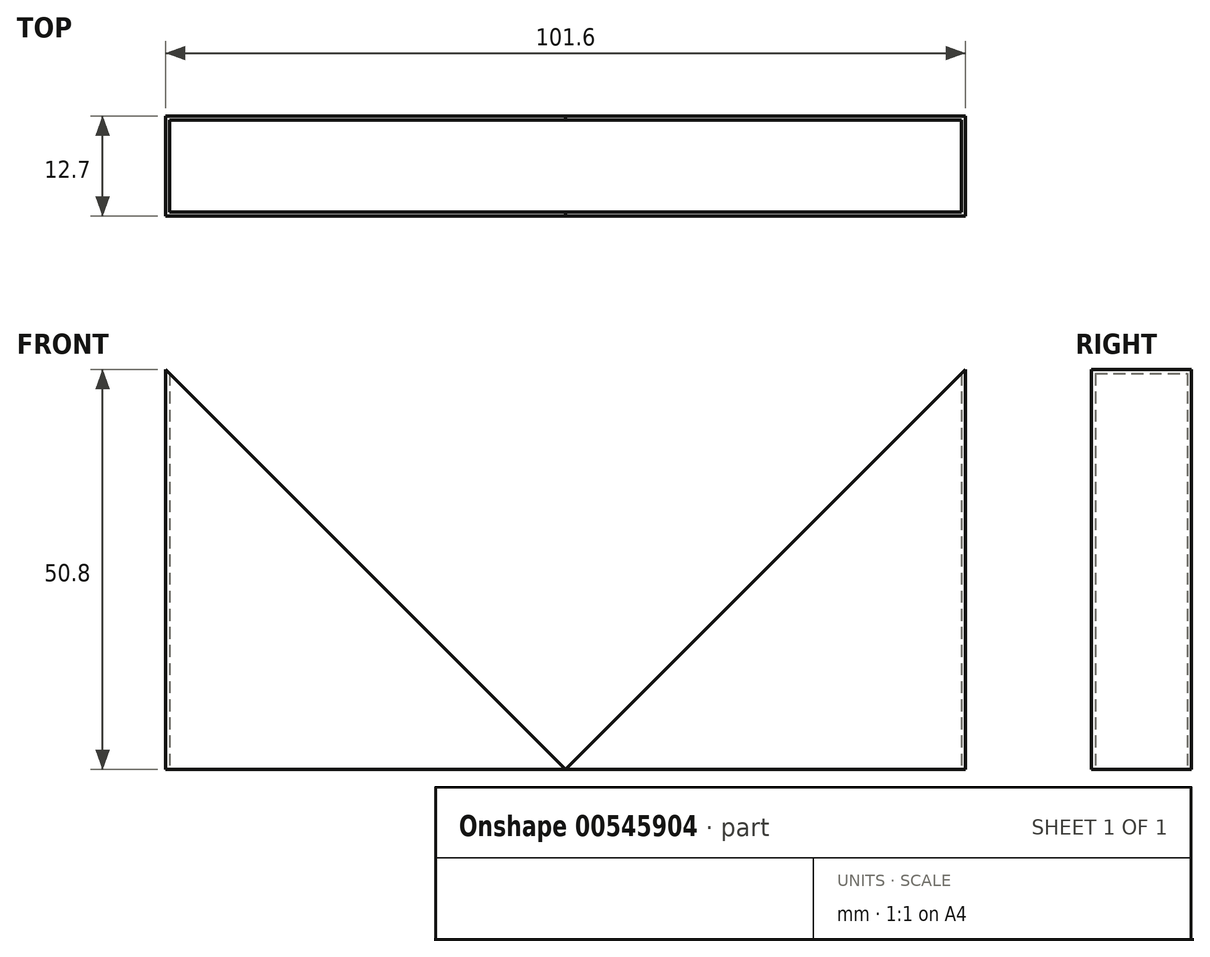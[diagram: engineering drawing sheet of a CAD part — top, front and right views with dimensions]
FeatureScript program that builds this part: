
annotation { "Feature Type Name" : "Feature", "Feature Type Description" : "" }
export const myFeature = defineFeature(function(context is Context, id is Id, definition is map)
    precondition{}
    {
        {
            var Q0;
            Q0=qCreatedBy(makeId("Top.planeOp"),FACE);
            var sketch = newSketch(context, id + "F0", { "sketchPlane" : qUnion([Q0])});
            skLineSegment(sketch, "E0.bottom", {"start": v(-50.8, -6.35) * mm, "end": v(50.8, -6.35) * mm});
            skLineSegment(sketch, "E0.top", {"start": v(-50.8, 6.35) * mm, "end": v(50.8, 6.35) * mm});
            skLineSegment(sketch, "E0.left", {"start": v(-50.8, -6.35) * mm, "end": v(-50.8, 6.35) * mm});
            skLineSegment(sketch, "E0.right", {"start": v(50.8, -6.35) * mm, "end": v(50.8, 6.35) * mm});
            skPoint(sketch, "E0.middle", {"position": v(0, 0) * mm});
            skSolve(sketch);
        }
        {
            var Q0;
            Q0 = qSketchRegion(id + "F0", true);
            extrude(context, id + "F1", {"entities" : qUnion([Q0]), "depth" : 50.8 * mm, "offsetDistance" : 25.4 * mm});
        }
        {
            var Q0;
            Q0=makeQuery(id+"F1.opExtrude","CAP_FACE",FACE,{"disambiguationData":[OSD([sQuery(id+"F0.wireOp",EDGE,"E0.bottom"),sQuery(id+"F0.wireOp",EDGE,"E0.top"),sQuery(id+"F0.wireOp",EDGE,"E0.left"),sQuery(id+"F0.wireOp",EDGE,"E0.right")])],"isStart":false});
            var Q1;
            Q1=makeQuery(id+"F1.opExtrude","CAP_FACE",FACE,{"disambiguationData":[OSD([sQuery(id+"F0.wireOp",EDGE,"E0.bottom"),sQuery(id+"F0.wireOp",EDGE,"E0.top"),sQuery(id+"F0.wireOp",EDGE,"E0.left"),sQuery(id+"F0.wireOp",EDGE,"E0.right")])],"isStart":true});
            shell(context, id + "F2", {"entities" : qUnion([Q0, Q1]), "thickness" : 0.5 * mm});
        }
        {
            var Q0;
            Q0=makeQuery(id+"F1.opExtrude","SWEPT_FACE",FACE,{"disambiguationData":[OSD([sQuery(id+"F0.wireOp",EDGE,"E0.bottom")])]});
            var sketch = newSketch(context, id + "F3", { "sketchPlane" : qUnion([Q0])});
            skLineSegment(sketch, "E1", {"start": v(0, 0) * mm, "end": v(-50.8, 50.8) * mm});
            skLineSegment(sketch, "E2", {"start": v(-50.8, 50.8) * mm, "end": v(50.8, 50.8) * mm});
            skLineSegment(sketch, "E3", {"start": v(50.8, 50.8) * mm, "end": v(0, 0) * mm});
            skSolve(sketch);
        }
        {
            var Q0;
            Q0 = qSketchRegion(id + "F3", true);
            extrude(context, id + "F4", {"entities" : qUnion([Q0]), "operationType" : NewBodyOperationType.REMOVE, "oppositeDirection" : true, "depth" : 13.2 * mm, "offsetDistance" : 25.4 * mm});
        }
    });
